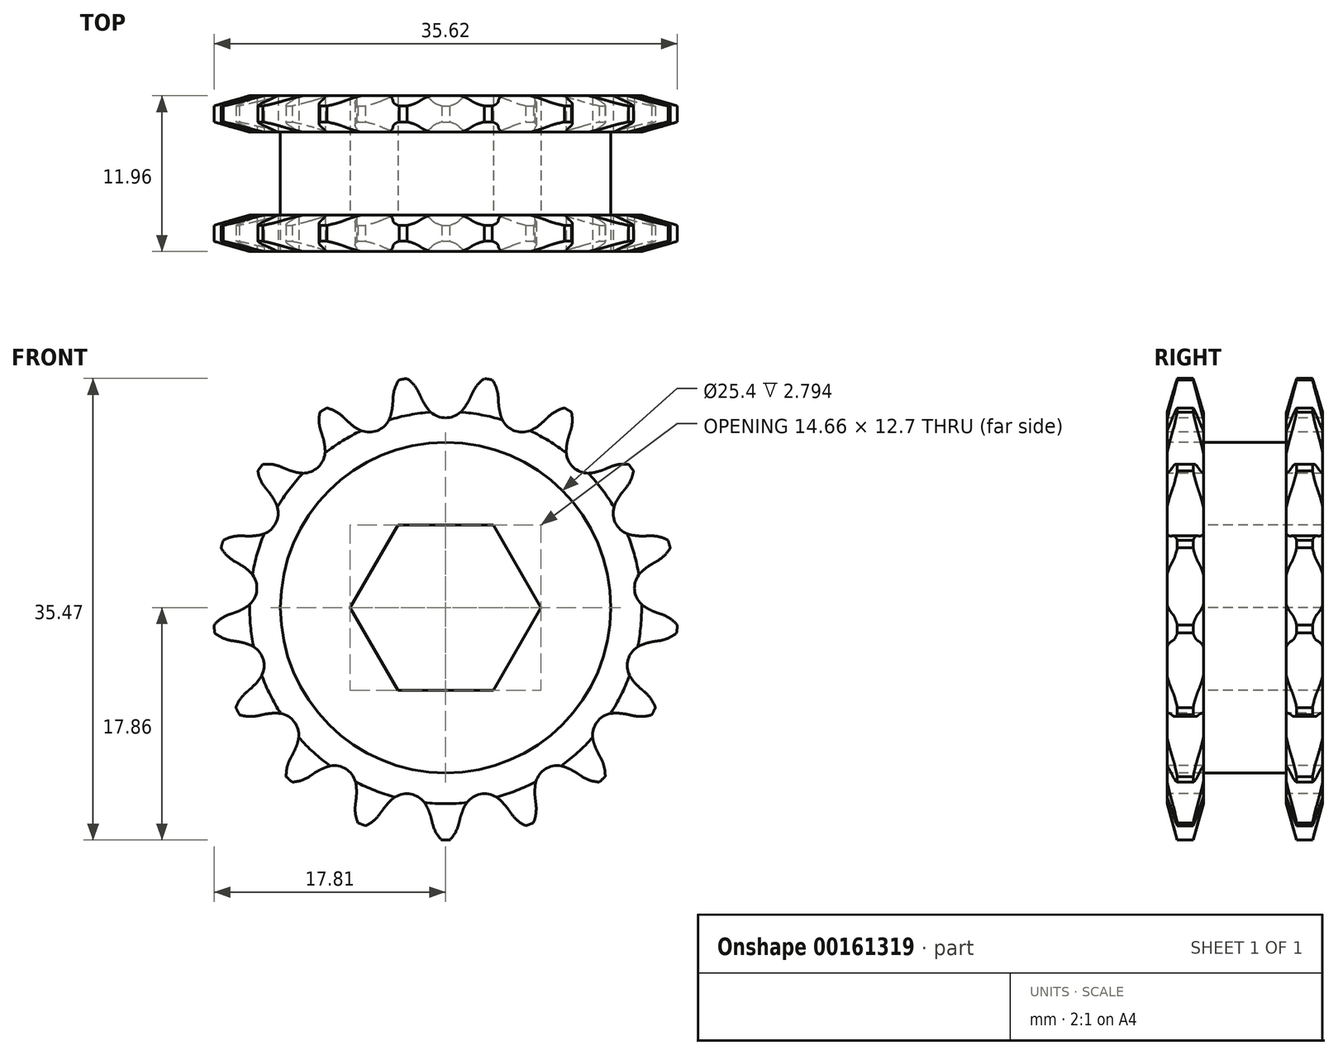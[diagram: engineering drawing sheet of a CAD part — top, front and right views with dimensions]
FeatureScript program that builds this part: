
annotation { "Feature Type Name" : "Feature", "Feature Type Description" : "" }
export const myFeature = defineFeature(function(context is Context, id is Id, definition is map)
    precondition{}
    {
        {
            var Q0;
            Q0=qCreatedBy(makeId("Right.planeOp"),FACE);
            var sketch = newSketch(context, id + "F0", { "sketchPlane" : qUnion([Q0])});
            skLineSegment(sketch, "E0", {"start": v(0, 0) * mm, "end": v(11.72, 0) * mm, "construction": true});
            skLineSegment(sketch, "E1.bottom", {"start": v(0, 3.18) * mm, "end": v(2.8, 3.18) * mm});
            skLineSegment(sketch, "E1.top", {"start": v(0, 17.86) * mm, "end": v(2.8, 17.86) * mm});
            skLineSegment(sketch, "E1.left", {"start": v(0, 3.18) * mm, "end": v(0, 17.86) * mm});
            skLineSegment(sketch, "E1.right", {"start": v(2.8, 3.18) * mm, "end": v(2.8, 17.86) * mm});
            skLineSegment(sketch, "E2.bottom", {"start": v(0, 3.18) * mm, "end": v(9.17, 3.18) * mm});
            skLineSegment(sketch, "E2.top", {"start": v(0, 12.7) * mm, "end": v(9.17, 12.7) * mm});
            skLineSegment(sketch, "E2.left", {"start": v(0, 3.18) * mm, "end": v(0, 12.7) * mm});
            skLineSegment(sketch, "E2.right", {"start": v(9.17, 3.18) * mm, "end": v(9.17, 12.7) * mm});
            skLineSegment(sketch, "E3.MirrorCS", {"start": v(0, -17.86) * mm, "end": v(2.8, -17.86) * mm});
            skLineSegment(sketch, "E4.MirrorCS", {"start": v(0, -3.18) * mm, "end": v(2.8, -3.18) * mm});
            skLineSegment(sketch, "E5.MirrorCS", {"start": v(9.17, -3.18) * mm, "end": v(9.17, -12.7) * mm});
            skLineSegment(sketch, "E6.MirrorCS", {"start": v(0, -3.18) * mm, "end": v(0, -17.86) * mm});
            skLineSegment(sketch, "E7.MirrorCS", {"start": v(2.8, -3.18) * mm, "end": v(2.8, -17.86) * mm});
            skLineSegment(sketch, "E8.MirrorCS", {"start": v(0, -3.18) * mm, "end": v(9.17, -3.18) * mm});
            skLineSegment(sketch, "E9.MirrorCS", {"start": v(0, -12.7) * mm, "end": v(9.17, -12.7) * mm});
            skLineSegment(sketch, "E10.MirrorCS", {"start": v(0, -3.18) * mm, "end": v(0, -12.7) * mm});
            skLineSegment(sketch, "E11.bottom", {"start": v(9.17, 3.18) * mm, "end": v(11.96, 3.18) * mm});
            skLineSegment(sketch, "E11.top", {"start": v(9.17, 17.86) * mm, "end": v(11.96, 17.86) * mm});
            skLineSegment(sketch, "E11.left", {"start": v(9.17, 3.18) * mm, "end": v(9.17, 17.86) * mm});
            skLineSegment(sketch, "E11.right", {"start": v(11.96, 3.18) * mm, "end": v(11.96, 17.86) * mm});
            skLineSegment(sketch, "E12.MirrorCS", {"start": v(9.17, -3.18) * mm, "end": v(9.17, -17.86) * mm});
            skLineSegment(sketch, "E13.MirrorCS", {"start": v(9.17, -17.86) * mm, "end": v(11.96, -17.86) * mm});
            skLineSegment(sketch, "E14.MirrorCS", {"start": v(11.96, -3.18) * mm, "end": v(11.96, -17.86) * mm});
            skLineSegment(sketch, "E15.MirrorCS", {"start": v(9.17, -3.18) * mm, "end": v(11.96, -3.18) * mm});
            skSolve(sketch);
        }
        {
            var Q0;
            {var subQ0=sQuery(id+"F0.wireOp",EDGE,"E1.top");Q0=makeQuery(id+"F0.imprint","IMPRINT",FACE,{"disambiguationData":[TD([[makeQuery(id+"F0.imprint","IMPRINT",EDGE,{"derivedFrom":subQ0}),-1.0]])]});}
            var Q1;
            {var subQ5=sQuery(id+"F0.wireOp",EDGE,"E2.left");Q1=makeQuery(id+"F0.imprint","IMPRINT",FACE,{"disambiguationData":[TD([[makeQuery(id+"F0.imprint","IMPRINT",EDGE,{"derivedFrom":subQ5}),-1.0]])]});}
            var Q2;
            {var subQ0=sQuery(id+"F0.wireOp",EDGE,"E2.bottom");var subQ1=sQuery(id+"F0.wireOp",EDGE,"E1.right");var subQ2=makeQuery(id+"F0.imprint","INTERSECT",VERTEX,{"derivedFrom":[subQ1,subQ0]});Q2=makeQuery(id+"F0.imprint","IMPRINT",FACE,{"disambiguationData":[TD([[makeQuery(id+"F0.imprint","IMPRINT",EDGE,{"disambiguationData":[TD([[subQ2,-1.0]])],"derivedFrom":subQ1}),-1.0]])]});}
            var Q3;
            {var subQ3=sQuery(id+"F0.wireOp",EDGE,"E11.bottom");Q3=makeQuery(id+"F0.imprint","IMPRINT",FACE,{"disambiguationData":[TD([[makeQuery(id+"F0.imprint","IMPRINT",EDGE,{"derivedFrom":subQ3}),1.0]])]});}
            var Q4;
            Q4=sQuery(id+"F0.wireOp",EDGE,"E0");
            revolve(context, id + "F1", {"entities" : qUnion([Q0, Q1, Q2, Q3]), "axis" : qUnion([Q4]), "revolveType" : RevolveType.FULL});
        }
        {
            var Q0;
            Q0=makeQuery(id+"F1.opRevolve","SWEPT_EDGE",EDGE,{"disambiguationData":[OSD([sQuery(id+"F0.wireOp",EDGE,"E1.top"),sQuery(id+"F0.wireOp",EDGE,"E1.left")])]});
            var Q1;
            Q1=makeQuery(id+"F1.opRevolve","SWEPT_EDGE",EDGE,{"disambiguationData":[OSD([sQuery(id+"F0.wireOp",EDGE,"E1.top"),sQuery(id+"F0.wireOp",EDGE,"E1.right")])]});
            chamfer(context, id + "F2", {"entities" : qUnion([Q0, Q1]), "chamferType" : ChamferType.TWO_OFFSETS, "width1" : 2.8 * mm, "oppositeDirection" : false, "width2" : 0.79 * mm, "tangentPropagation" : true});
        }
        {
            var Q0;
            Q0=makeQuery(id+"F1.opRevolve","SWEPT_EDGE",EDGE,{"disambiguationData":[OSD([sQuery(id+"F0.wireOp",EDGE,"E11.top"),sQuery(id+"F0.wireOp",EDGE,"E11.right")])]});
            var Q1;
            Q1=makeQuery(id+"F1.opRevolve","SWEPT_EDGE",EDGE,{"disambiguationData":[OSD([sQuery(id+"F0.wireOp",EDGE,"E11.top"),sQuery(id+"F0.wireOp",EDGE,"E11.left")])]});
            chamfer(context, id + "F3", {"entities" : qUnion([Q0, Q1]), "chamferType" : ChamferType.TWO_OFFSETS, "width1" : 2.8 * mm, "oppositeDirection" : true, "width2" : 0.79 * mm, "tangentPropagation" : true});
        }
        {
            var Q0;
            Q0=makeQuery(id+"F1.opRevolve","SWEPT_FACE",FACE,{"disambiguationData":[OSD([sQuery(id+"F0.wireOp",EDGE,"E1.left"),sQuery(id+"F0.wireOp",EDGE,"E2.left")])]});
            var sketch = newSketch(context, id + "F4", { "sketchPlane" : qUnion([Q0])});
            skCircle(sketch, "E16", {"center": v(0, 0) * mm, "radius": 16.28 * mm, "construction": true});
            skLineSegment(sketch, "E17", {"start": v(0, 0) * mm, "end": v(0, 16.28) * mm, "construction": true});
            skLineSegment(sketch, "E18", {"start": v(0, 16.28) * mm, "end": v(74.18, 16.28) * mm, "construction": true});
            skLineSegment(sketch, "E19", {"start": v(0, 16.28) * mm, "end": v(2.06, 17.93) * mm, "construction": true});
            skLineSegment(sketch, "E20", {"start": v(2.06, 17.93) * mm, "end": v(-1.9, 16.15) * mm, "construction": true});
            skLineSegment(sketch, "E21", {"start": v(-1.9, 16.15) * mm, "end": v(-2.05, 16.5) * mm});
            skLineSegment(sketch, "E22", {"start": v(0, 0) * mm, "end": v(-3.56, 17.92) * mm, "construction": true});
            skArc(sketch, "E23", {"start": v(-3.56, 17.92) * mm, "mid": v(-6.4, 13.4) * mm, "end": v(-2.05, 16.5) * mm, "construction": true});
            skArc(sketch, "E24", {"start": v(-2.05, 16.5) * mm, "mid": v(-2.67, 17.35) * mm, "end": v(-3.56, 17.92) * mm});
            skLineSegment(sketch, "E25", {"start": v(13.7, -18.46) * mm, "end": v(-1.9, 16.16) * mm, "construction": true});
            skArc(sketch, "E26", {"start": v(-1.9, 16.15) * mm, "mid": v(-1.64, 15.66) * mm, "end": v(-1.32, 15.21) * mm});
            skArc(sketch, "E27", {"start": v(-1.32, 15.21) * mm, "mid": v(5.76, 20.2) * mm, "end": v(-1.9, 16.15) * mm, "construction": true});
            skArc(sketch, "E28.0.MirrorCS", {"start": v(1.9, 16.15) * mm, "mid": v(1.64, 15.66) * mm, "end": v(1.32, 15.21) * mm});
            skLineSegment(sketch, "E29.0.MirrorCS", {"start": v(1.9, 16.15) * mm, "end": v(2.05, 16.5) * mm});
            skArc(sketch, "E30.0.MirrorCS", {"start": v(2.05, 16.5) * mm, "mid": v(2.67, 17.35) * mm, "end": v(3.56, 17.92) * mm});
            skArc(sketch, "E31", {"start": v(-1.32, 15.21) * mm, "mid": v(0, 14.58) * mm, "end": v(1.32, 15.21) * mm});
            skArc(sketch, "E32", {"start": v(1.32, 15.21) * mm, "mid": v(0, 17.97) * mm, "end": v(-1.32, 15.21) * mm, "construction": true});
            skArc(sketch, "E33.1.0", {"start": v(-7.87, 14.64) * mm, "mid": v(-8.76, 15.22) * mm, "end": v(-9.8, 15.42) * mm});
            skLineSegment(sketch, "E33.1.1", {"start": v(-7.6, 14.37) * mm, "end": v(-7.87, 14.64) * mm});
            skArc(sketch, "E33.1.2", {"start": v(-7.6, 14.37) * mm, "mid": v(-7.19, 14.01) * mm, "end": v(-6.73, 13.7) * mm});
            skArc(sketch, "E33.1.3", {"start": v(-6.73, 13.7) * mm, "mid": v(-5.27, 13.6) * mm, "end": v(-4.26, 14.66) * mm});
            skArc(sketch, "E33.1.4", {"start": v(-4.06, 15.74) * mm, "mid": v(-4.13, 15.2) * mm, "end": v(-4.26, 14.66) * mm});
            skLineSegment(sketch, "E33.1.5", {"start": v(-4.06, 15.74) * mm, "end": v(-4.04, 16.12) * mm});
            skArc(sketch, "E33.1.6", {"start": v(-4.04, 16.12) * mm, "mid": v(-3.78, 17.15) * mm, "end": v(-3.15, 18) * mm});
            skArc(sketch, "E33.2.0", {"start": v(-12.63, 10.8) * mm, "mid": v(-13.66, 11.03) * mm, "end": v(-14.7, 10.84) * mm});
            skLineSegment(sketch, "E33.2.1", {"start": v(-12.28, 10.65) * mm, "end": v(-12.63, 10.8) * mm});
            skArc(sketch, "E33.2.2", {"start": v(-12.28, 10.65) * mm, "mid": v(-11.76, 10.47) * mm, "end": v(-11.23, 10.35) * mm});
            skArc(sketch, "E33.2.3", {"start": v(-11.23, 10.35) * mm, "mid": v(-9.82, 10.77) * mm, "end": v(-9.27, 12.13) * mm});
            skArc(sketch, "E33.2.4", {"start": v(-9.48, 13.2) * mm, "mid": v(-9.34, 12.68) * mm, "end": v(-9.27, 12.13) * mm});
            skLineSegment(sketch, "E33.2.5", {"start": v(-9.48, 13.2) * mm, "end": v(-9.6, 13.57) * mm});
            skArc(sketch, "E33.2.6", {"start": v(-9.6, 13.57) * mm, "mid": v(-9.72, 14.62) * mm, "end": v(-9.44, 15.64) * mm});
            skArc(sketch, "E33.3.0", {"start": v(-15.68, 5.51) * mm, "mid": v(-16.72, 5.35) * mm, "end": v(-17.63, 4.8) * mm});
            skLineSegment(sketch, "E33.3.1", {"start": v(-15.3, 5.5) * mm, "end": v(-15.68, 5.51) * mm});
            skArc(sketch, "E33.3.2", {"start": v(-15.3, 5.5) * mm, "mid": v(-14.75, 5.51) * mm, "end": v(-14.2, 5.6) * mm});
            skArc(sketch, "E33.3.3", {"start": v(-14.2, 5.6) * mm, "mid": v(-13.05, 6.5) * mm, "end": v(-13.03, 7.97) * mm});
            skArc(sketch, "E33.3.4", {"start": v(-13.6, 8.9) * mm, "mid": v(-13.29, 8.45) * mm, "end": v(-13.03, 7.97) * mm});
            skLineSegment(sketch, "E33.3.5", {"start": v(-13.6, 8.9) * mm, "end": v(-13.85, 9.19) * mm});
            skArc(sketch, "E33.3.6", {"start": v(-13.85, 9.19) * mm, "mid": v(-14.35, 10.12) * mm, "end": v(-14.45, 11.18) * mm});
            skArc(sketch, "E33.4.0", {"start": v(-16.61, -0.52) * mm, "mid": v(-17.53, -1.05) * mm, "end": v(-18.17, -1.9) * mm});
            skLineSegment(sketch, "E33.4.1", {"start": v(-16.25, -0.4) * mm, "end": v(-16.61, -0.52) * mm});
            skArc(sketch, "E33.4.2", {"start": v(-16.25, -0.4) * mm, "mid": v(-15.75, -0.19) * mm, "end": v(-15.27, 0.09) * mm});
            skArc(sketch, "E33.4.3", {"start": v(-15.27, 0.09) * mm, "mid": v(-14.51, 1.35) * mm, "end": v(-15.03, 2.72) * mm});
            skArc(sketch, "E33.4.4", {"start": v(-15.9, 3.38) * mm, "mid": v(-15.44, 3.08) * mm, "end": v(-15.03, 2.72) * mm});
            skLineSegment(sketch, "E33.4.5", {"start": v(-15.9, 3.38) * mm, "end": v(-16.23, 3.57) * mm});
            skArc(sketch, "E33.4.6", {"start": v(-16.23, 3.57) * mm, "mid": v(-17.03, 4.26) * mm, "end": v(-17.51, 5.2) * mm});
            skArc(sketch, "E33.5.0", {"start": v(-15.3, -6.49) * mm, "mid": v(-15.96, -7.31) * mm, "end": v(-16.26, -8.33) * mm});
            skLineSegment(sketch, "E33.5.1", {"start": v(-15.01, -6.24) * mm, "end": v(-15.3, -6.49) * mm});
            skArc(sketch, "E33.5.2", {"start": v(-15.01, -6.24) * mm, "mid": v(-14.61, -5.86) * mm, "end": v(-14.27, -5.44) * mm});
            skArc(sketch, "E33.5.3", {"start": v(-14.27, -5.44) * mm, "mid": v(-14.02, -3.99) * mm, "end": v(-15, -2.89) * mm});
            skArc(sketch, "E33.5.4", {"start": v(-16.05, -2.6) * mm, "mid": v(-15.51, -2.7) * mm, "end": v(-15, -2.89) * mm});
            skLineSegment(sketch, "E33.5.5", {"start": v(-16.05, -2.6) * mm, "end": v(-16.42, -2.54) * mm});
            skArc(sketch, "E33.5.6", {"start": v(-16.42, -2.54) * mm, "mid": v(-17.42, -2.18) * mm, "end": v(-18.2, -1.48) * mm});
            skArc(sketch, "E33.6.0", {"start": v(-11.92, -11.58) * mm, "mid": v(-12.24, -12.59) * mm, "end": v(-12.15, -13.64) * mm});
            skLineSegment(sketch, "E33.6.1", {"start": v(-11.74, -11.24) * mm, "end": v(-11.92, -11.58) * mm});
            skArc(sketch, "E33.6.2", {"start": v(-11.74, -11.24) * mm, "mid": v(-11.5, -10.75) * mm, "end": v(-11.34, -10.22) * mm});
            skArc(sketch, "E33.6.3", {"start": v(-11.34, -10.22) * mm, "mid": v(-11.63, -8.78) * mm, "end": v(-12.94, -8.11) * mm});
            skArc(sketch, "E33.6.4", {"start": v(-14.03, -8.22) * mm, "mid": v(-13.49, -8.13) * mm, "end": v(-12.94, -8.11) * mm});
            skLineSegment(sketch, "E33.6.5", {"start": v(-14.03, -8.22) * mm, "end": v(-14.4, -8.3) * mm});
            skArc(sketch, "E33.6.6", {"start": v(-14.4, -8.3) * mm, "mid": v(-15.46, -8.33) * mm, "end": v(-16.45, -7.95) * mm});
            skArc(sketch, "E33.7.0", {"start": v(-6.94, -15.1) * mm, "mid": v(-6.87, -16.16) * mm, "end": v(-6.4, -17.1) * mm});
            skLineSegment(sketch, "E33.7.1", {"start": v(-6.89, -14.73) * mm, "end": v(-6.94, -15.1) * mm});
            skArc(sketch, "E33.7.2", {"start": v(-6.89, -14.73) * mm, "mid": v(-6.85, -14.18) * mm, "end": v(-6.88, -13.63) * mm});
            skArc(sketch, "E33.7.3", {"start": v(-6.88, -13.63) * mm, "mid": v(-7.67, -12.4) * mm, "end": v(-9.13, -12.24) * mm});
            skArc(sketch, "E33.7.4", {"start": v(-10.11, -12.73) * mm, "mid": v(-9.64, -12.45) * mm, "end": v(-9.13, -12.24) * mm});
            skLineSegment(sketch, "E33.7.5", {"start": v(-10.11, -12.73) * mm, "end": v(-10.43, -12.94) * mm});
            skArc(sketch, "E33.7.6", {"start": v(-10.43, -12.94) * mm, "mid": v(-11.4, -13.35) * mm, "end": v(-12.46, -13.36) * mm});
            skArc(sketch, "E33.8.0", {"start": v(-1.01, -16.59) * mm, "mid": v(-0.57, -17.55) * mm, "end": v(0.21, -18.27) * mm});
            skLineSegment(sketch, "E33.8.1", {"start": v(-1.1, -16.22) * mm, "end": v(-1.01, -16.59) * mm});
            skArc(sketch, "E33.8.2", {"start": v(-1.1, -16.22) * mm, "mid": v(-1.27, -15.7) * mm, "end": v(-1.5, -15.2) * mm});
            skArc(sketch, "E33.8.3", {"start": v(-1.5, -15.2) * mm, "mid": v(-2.68, -14.33) * mm, "end": v(-4.1, -14.7) * mm});
            skArc(sketch, "E33.8.4", {"start": v(-4.83, -15.52) * mm, "mid": v(-4.49, -15.1) * mm, "end": v(-4.1, -14.7) * mm});
            skLineSegment(sketch, "E33.8.5", {"start": v(-4.83, -15.52) * mm, "end": v(-5.05, -15.83) * mm});
            skArc(sketch, "E33.8.6", {"start": v(-5.05, -15.83) * mm, "mid": v(-5.81, -16.57) * mm, "end": v(-6.8, -16.96) * mm});
            skArc(sketch, "E33.9.0", {"start": v(5.05, -15.83) * mm, "mid": v(5.81, -16.57) * mm, "end": v(6.8, -16.96) * mm});
            skLineSegment(sketch, "E33.9.1", {"start": v(4.83, -15.52) * mm, "end": v(5.05, -15.83) * mm});
            skArc(sketch, "E33.9.2", {"start": v(4.83, -15.52) * mm, "mid": v(4.49, -15.1) * mm, "end": v(4.1, -14.7) * mm});
            skArc(sketch, "E33.9.3", {"start": v(4.1, -14.7) * mm, "mid": v(2.68, -14.33) * mm, "end": v(1.5, -15.2) * mm});
            skArc(sketch, "E33.9.4", {"start": v(1.1, -16.22) * mm, "mid": v(1.27, -15.7) * mm, "end": v(1.5, -15.2) * mm});
            skLineSegment(sketch, "E33.9.5", {"start": v(1.1, -16.22) * mm, "end": v(1.01, -16.59) * mm});
            skArc(sketch, "E33.9.6", {"start": v(1.01, -16.59) * mm, "mid": v(0.57, -17.55) * mm, "end": v(-0.21, -18.27) * mm});
            skArc(sketch, "E33.10.0", {"start": v(10.43, -12.94) * mm, "mid": v(11.4, -13.35) * mm, "end": v(12.46, -13.36) * mm});
            skLineSegment(sketch, "E33.10.1", {"start": v(10.11, -12.73) * mm, "end": v(10.43, -12.94) * mm});
            skArc(sketch, "E33.10.2", {"start": v(10.11, -12.73) * mm, "mid": v(9.64, -12.45) * mm, "end": v(9.13, -12.24) * mm});
            skArc(sketch, "E33.10.3", {"start": v(9.13, -12.24) * mm, "mid": v(7.67, -12.4) * mm, "end": v(6.88, -13.63) * mm});
            skArc(sketch, "E33.10.4", {"start": v(6.89, -14.73) * mm, "mid": v(6.85, -14.18) * mm, "end": v(6.88, -13.63) * mm});
            skLineSegment(sketch, "E33.10.5", {"start": v(6.89, -14.73) * mm, "end": v(6.94, -15.1) * mm});
            skArc(sketch, "E33.10.6", {"start": v(6.94, -15.1) * mm, "mid": v(6.87, -16.16) * mm, "end": v(6.4, -17.1) * mm});
            skArc(sketch, "E33.11.0", {"start": v(14.4, -8.3) * mm, "mid": v(15.46, -8.33) * mm, "end": v(16.45, -7.95) * mm});
            skLineSegment(sketch, "E33.11.1", {"start": v(14.03, -8.22) * mm, "end": v(14.4, -8.3) * mm});
            skArc(sketch, "E33.11.2", {"start": v(14.03, -8.22) * mm, "mid": v(13.49, -8.13) * mm, "end": v(12.94, -8.11) * mm});
            skArc(sketch, "E33.11.3", {"start": v(12.94, -8.11) * mm, "mid": v(11.63, -8.78) * mm, "end": v(11.34, -10.22) * mm});
            skArc(sketch, "E33.11.4", {"start": v(11.74, -11.24) * mm, "mid": v(11.5, -10.75) * mm, "end": v(11.34, -10.22) * mm});
            skLineSegment(sketch, "E33.11.5", {"start": v(11.74, -11.24) * mm, "end": v(11.92, -11.58) * mm});
            skArc(sketch, "E33.11.6", {"start": v(11.92, -11.58) * mm, "mid": v(12.24, -12.59) * mm, "end": v(12.15, -13.64) * mm});
            skArc(sketch, "E33.12.0", {"start": v(16.42, -2.54) * mm, "mid": v(17.42, -2.18) * mm, "end": v(18.2, -1.48) * mm});
            skLineSegment(sketch, "E33.12.1", {"start": v(16.05, -2.6) * mm, "end": v(16.42, -2.54) * mm});
            skArc(sketch, "E33.12.2", {"start": v(16.05, -2.6) * mm, "mid": v(15.51, -2.7) * mm, "end": v(15, -2.89) * mm});
            skArc(sketch, "E33.12.3", {"start": v(15, -2.89) * mm, "mid": v(14.02, -3.99) * mm, "end": v(14.27, -5.44) * mm});
            skArc(sketch, "E33.12.4", {"start": v(15.01, -6.24) * mm, "mid": v(14.61, -5.86) * mm, "end": v(14.27, -5.44) * mm});
            skLineSegment(sketch, "E33.12.5", {"start": v(15.01, -6.24) * mm, "end": v(15.3, -6.49) * mm});
            skArc(sketch, "E33.12.6", {"start": v(15.3, -6.49) * mm, "mid": v(15.96, -7.31) * mm, "end": v(16.26, -8.33) * mm});
            skArc(sketch, "E33.13.0", {"start": v(16.23, 3.57) * mm, "mid": v(17.03, 4.26) * mm, "end": v(17.51, 5.2) * mm});
            skLineSegment(sketch, "E33.13.1", {"start": v(15.9, 3.38) * mm, "end": v(16.23, 3.57) * mm});
            skArc(sketch, "E33.13.2", {"start": v(15.9, 3.38) * mm, "mid": v(15.44, 3.08) * mm, "end": v(15.03, 2.72) * mm});
            skArc(sketch, "E33.13.3", {"start": v(15.03, 2.72) * mm, "mid": v(14.51, 1.35) * mm, "end": v(15.27, 0.09) * mm});
            skArc(sketch, "E33.13.4", {"start": v(16.25, -0.4) * mm, "mid": v(15.75, -0.19) * mm, "end": v(15.27, 0.09) * mm});
            skLineSegment(sketch, "E33.13.5", {"start": v(16.25, -0.4) * mm, "end": v(16.61, -0.52) * mm});
            skArc(sketch, "E33.13.6", {"start": v(16.61, -0.52) * mm, "mid": v(17.53, -1.05) * mm, "end": v(18.17, -1.9) * mm});
            skArc(sketch, "E33.14.0", {"start": v(13.85, 9.19) * mm, "mid": v(14.35, 10.12) * mm, "end": v(14.45, 11.18) * mm});
            skLineSegment(sketch, "E33.14.1", {"start": v(13.6, 8.9) * mm, "end": v(13.85, 9.19) * mm});
            skArc(sketch, "E33.14.2", {"start": v(13.6, 8.9) * mm, "mid": v(13.29, 8.45) * mm, "end": v(13.03, 7.97) * mm});
            skArc(sketch, "E33.14.3", {"start": v(13.03, 7.97) * mm, "mid": v(13.05, 6.5) * mm, "end": v(14.2, 5.6) * mm});
            skArc(sketch, "E33.14.4", {"start": v(15.3, 5.5) * mm, "mid": v(14.75, 5.51) * mm, "end": v(14.2, 5.6) * mm});
            skLineSegment(sketch, "E33.14.5", {"start": v(15.3, 5.5) * mm, "end": v(15.68, 5.51) * mm});
            skArc(sketch, "E33.14.6", {"start": v(15.68, 5.51) * mm, "mid": v(16.72, 5.35) * mm, "end": v(17.63, 4.8) * mm});
            skArc(sketch, "E33.15.0", {"start": v(9.6, 13.57) * mm, "mid": v(9.72, 14.62) * mm, "end": v(9.44, 15.64) * mm});
            skLineSegment(sketch, "E33.15.1", {"start": v(9.48, 13.2) * mm, "end": v(9.6, 13.57) * mm});
            skArc(sketch, "E33.15.2", {"start": v(9.48, 13.2) * mm, "mid": v(9.34, 12.68) * mm, "end": v(9.27, 12.13) * mm});
            skArc(sketch, "E33.15.3", {"start": v(9.27, 12.13) * mm, "mid": v(9.82, 10.77) * mm, "end": v(11.23, 10.35) * mm});
            skArc(sketch, "E33.15.4", {"start": v(12.28, 10.65) * mm, "mid": v(11.76, 10.47) * mm, "end": v(11.23, 10.35) * mm});
            skLineSegment(sketch, "E33.15.5", {"start": v(12.28, 10.65) * mm, "end": v(12.63, 10.8) * mm});
            skArc(sketch, "E33.15.6", {"start": v(12.63, 10.8) * mm, "mid": v(13.66, 11.03) * mm, "end": v(14.7, 10.84) * mm});
            skArc(sketch, "E34.1.16.0", {"start": v(4.04, 16.12) * mm, "mid": v(3.78, 17.15) * mm, "end": v(3.15, 18) * mm});
            skLineSegment(sketch, "E34.4.16.0", {"start": v(4.06, 15.74) * mm, "end": v(4.04, 16.12) * mm});
            skArc(sketch, "E34.7.16.0", {"start": v(4.06, 15.74) * mm, "mid": v(4.13, 15.2) * mm, "end": v(4.26, 14.66) * mm});
            skArc(sketch, "E34.11.16.0", {"start": v(4.26, 14.66) * mm, "mid": v(5.27, 13.6) * mm, "end": v(6.73, 13.7) * mm});
            skArc(sketch, "E34.15.16.0", {"start": v(7.6, 14.37) * mm, "mid": v(7.19, 14.01) * mm, "end": v(6.73, 13.7) * mm});
            skLineSegment(sketch, "E34.19.16.0", {"start": v(7.6, 14.37) * mm, "end": v(7.87, 14.64) * mm});
            skArc(sketch, "E34.22.16.0", {"start": v(7.87, 14.64) * mm, "mid": v(8.76, 15.22) * mm, "end": v(9.8, 15.42) * mm});
            skSolve(sketch);
        }
        {
            var Q0;
            Q0 = qSketchRegion(id + "F4", true);
            extrude(context, id + "F5", {"entities" : qUnion([Q0]), "operationType" : NewBodyOperationType.INTERSECT, "endBound" : BoundingType.THROUGH_ALL, "oppositeDirection" : true, "depth" : 25.4 * mm});
        }
        {
            var Q0;
            Q0=makeQuery(id+"F1.opRevolve","SWEPT_FACE",FACE,{"disambiguationData":[OSD([sQuery(id+"F0.wireOp",EDGE,"E1.left"),sQuery(id+"F0.wireOp",EDGE,"E2.left")])]});
            var sketch = newSketch(context, id + "F6", { "sketchPlane" : qUnion([Q0])});
            skCircle(sketch, "E35.cCircle", {"center": v(0, 0) * mm, "radius": 6.35 * mm, "construction": true});
            skLineSegment(sketch, "E35.0", {"start": v(-3.67, 6.35) * mm, "end": v(3.67, 6.35) * mm});
            skLineSegment(sketch, "E35.1", {"start": v(3.67, 6.35) * mm, "end": v(7.33, 0) * mm});
            skLineSegment(sketch, "E35.2", {"start": v(7.33, 0) * mm, "end": v(3.67, -6.35) * mm});
            skLineSegment(sketch, "E35.3", {"start": v(3.67, -6.35) * mm, "end": v(-3.67, -6.35) * mm});
            skLineSegment(sketch, "E35.4", {"start": v(-3.67, -6.35) * mm, "end": v(-7.33, 0) * mm});
            skLineSegment(sketch, "E35.5", {"start": v(-7.33, 0) * mm, "end": v(-3.67, 6.35) * mm});
            skPoint(sketch, "E35.0.midPoint", {"position": v(0, 6.35) * mm});
            skSolve(sketch);
        }
        {
            var Q0;
            Q0 = qSketchRegion(id + "F6", true);
            extrude(context, id + "F7", {"entities" : qUnion([Q0]), "operationType" : NewBodyOperationType.REMOVE, "endBound" : BoundingType.THROUGH_ALL, "oppositeDirection" : true, "depth" : 25.4 * mm});
        }
    });
